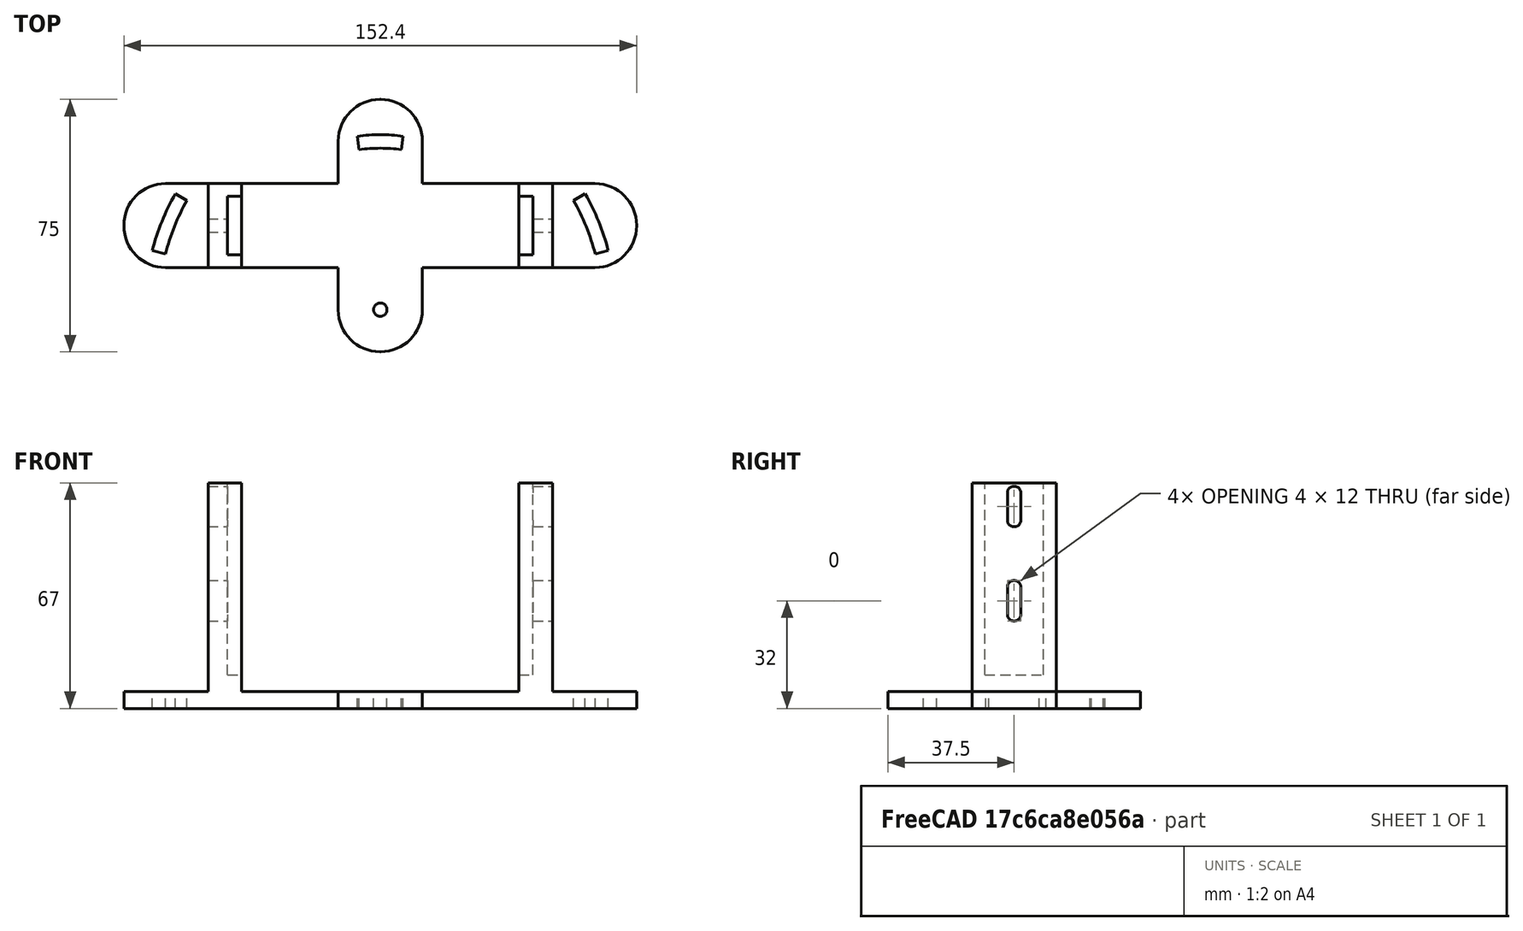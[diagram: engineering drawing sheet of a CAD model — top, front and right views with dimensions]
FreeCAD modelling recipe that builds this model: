
FCSTD DOCUMENT  (FreeCAD 0.18R4 (GitTag))
Label: Kamerhalter_Teil_4
License: All rights reserved
LicenseURL: http://en.wikipedia.org/wiki/All_rights_reserved
objects: Part::Box×10, Part::Cylinder×7, Part::Cut×6, Part::Fillet×6, Part::MultiFuse×5
note: 34 computed .brp shape members not serialized (recipe doc carries the construction recipe); baked Part::Feature solids carry a one-line shape summary decoded from their .brp

FEATURE [Part::Cylinder] Cylinder001  label="Zylinder001"
  Angle = 15
  AttacherType = Attacher::AttachEngine3D
  Height = 5
  Placement = pos=(0,0,0) rot=(0,0,1;0.253073rad)
  Radius = 70
FEATURE [Part::Cylinder] Cylinder002  label="Zylinder002"
  Angle = 15
  AttacherType = Attacher::AttachEngine3D
  Height = 5
  Placement = pos=(0,0,0) rot=(0,0,1;0.253073rad)
  Radius = 66
FEATURE [Part::Cut] Cut  label="Bohrschlitz001"
  Base = -> Cylinder001
  Tool = -> Cylinder002
FEATURE [Part::Cylinder] Cylinder003  label="Zylinder003"
  Angle = 15
  AttacherType = Attacher::AttachEngine3D
  Height = 5
  Placement = pos=(0,0,0) rot=(0,0,1;1.4399rad)
  Radius = 52
FEATURE [Part::Cylinder] Cylinder004  label="Zylinder004"
  Angle = 15
  AttacherType = Attacher::AttachEngine3D
  Height = 5
  Placement = pos=(0,0,0) rot=(0,0,1;1.4399rad)
  Radius = 48
FEATURE [Part::Cut] Cut001  label="Bohrschlitz002"
  Base = -> Cylinder003
  Tool = -> Cylinder004
FEATURE [Part::Cylinder] Cylinder005  label="Zylinder005"
  Angle = 15
  AttacherType = Attacher::AttachEngine3D
  Height = 5
  Placement = pos=(0,0,0) rot=(0,0,1;2.62672rad)
  Radius = 70
FEATURE [Part::Cylinder] Cylinder006  label="Zylinder006"
  Angle = 15
  AttacherType = Attacher::AttachEngine3D
  Height = 5
  Placement = pos=(0,0,0) rot=(0,0,1;2.62672rad)
  Radius = 66
FEATURE [Part::Cut] Cut002  label="Bohrschlitz003"
  Base = -> Cylinder005
  Tool = -> Cylinder006
FEATURE [Part::Box] Box006  label="Würfel006"
  AttacherType = Attacher::AttachEngine3D
  Height = 67
  Length = 10
  Placement = pos=(35,12.5,0) rot=(0,0,1;0rad)
  Width = 25
FEATURE [Part::Box] Box007  label="Würfel007"
  AttacherType = Attacher::AttachEngine3D
  Height = 67
  Length = 4.2
  Placement = pos=(35,16.3,10) rot=(0,0,1;0rad)
  Width = 17.4
FEATURE [Part::Box] Box008  label="Würfel008"
  AttacherType = Attacher::AttachEngine3D
  Height = 12
  Length = 6
  Placement = pos=(39,23,54) rot=(0,0,1;0rad)
  Width = 4
FEATURE [Part::Box] Box009  label="Würfel009"
  AttacherType = Attacher::AttachEngine3D
  Height = 12
  Length = 6
  Placement = pos=(39,23,26) rot=(0,0,1;0rad)
  Width = 4
FEATURE [Part::Fillet] Fillet006
  Base = -> Box008
  Edges = 4 edges r=1.9: [Edge9,Edge10,Edge11,Edge12]
FEATURE [Part::Fillet] Fillet007
  Base = -> Box009
  Edges = 4 edges r=1.9: [Edge9,Edge10,Edge11,Edge12]
FEATURE [Part::Box] Box010  label="Würfel010"
  AttacherType = Attacher::AttachEngine3D
  Height = 12
  Length = 6
  Placement = pos=(-45,23,54) rot=(0,0,1;0rad)
  Width = 4
FEATURE [Part::Box] Box011  label="Würfel011"
  AttacherType = Attacher::AttachEngine3D
  Height = 12
  Length = 6
  Placement = pos=(-45,23,26) rot=(0,0,1;0rad)
  Width = 4
FEATURE [Part::Fillet] Fillet008
  Base = -> Box010
  Edges = 4 edges r=1.9: [Edge9,Edge10,Edge11,Edge12]
FEATURE [Part::Fillet] Fillet009
  Base = -> Box011
  Edges = 4 edges r=1.9: [Edge9,Edge10,Edge11,Edge12]
FEATURE [Part::Box] Box012  label="Würfel012"
  AttacherType = Attacher::AttachEngine3D
  Height = 67
  Length = 10
  Placement = pos=(-45,12.5,0) rot=(0,0,1;0rad)
  Width = 25
FEATURE [Part::Box] Box013  label="Würfel013"
  AttacherType = Attacher::AttachEngine3D
  Height = 67
  Length = 4.2
  Placement = pos=(-39.2,16.3,10) rot=(0,0,1;0rad)
  Width = 17.4
FEATURE [Part::MultiFuse] Fusion002
  Shapes = -> [Fillet007,Box007,Fillet006]
FEATURE [Part::Cut] Cut005  label="Stuetze001"
  Base = -> Box006
  Placement = pos=(6.2,0,0) rot=(0,0,1;0rad)
  Tool = -> Fusion002
FEATURE [Part::MultiFuse] Fusion003
  Shapes = -> [Fillet008,Fillet009,Box013]
FEATURE [Part::Cut] Cut006  label="Stuetze002"
  Base = -> Box012
  Placement = pos=(-6.2,0,0) rot=(0,0,1;0rad)
  Tool = -> Fusion003
FEATURE [Part::Box] Box014  label="Würfel014"
  AttacherType = Attacher::AttachEngine3D
  Height = 5
  Length = 152.4
  Placement = pos=(-76.2,12.5,0) rot=(0,0,1;0rad)
  Width = 25
FEATURE [Part::Fillet] Fillet010  label="Fillet001"
  Base = -> Box014
  Edges = 4 edges r=12.4: [Edge1,Edge3,Edge5,Edge7]
FEATURE [Part::Box] Box015  label="Würfel015"
  AttacherType = Attacher::AttachEngine3D
  Height = 5
  Length = 25
  Placement = pos=(-12.5,-12.5,0) rot=(0,0,1;0rad)
  Width = 75
FEATURE [Part::Fillet] Fillet011  label="Fillet002"
  Base = -> Box015
  Edges = 4 edges r=12.4: [Edge1,Edge3,Edge5,Edge7]
FEATURE [Part::MultiFuse] Fusion005  label="Sockel"
  Shapes = -> [Fillet010,Fillet011]
FEATURE [Part::Cylinder] Cylinder007  label="Borhloch002"
  Angle = 360
  AttacherType = Attacher::AttachEngine3D
  Height = 5
  Radius = 2
FEATURE [Part::MultiFuse] Fusion004  label="Bohrschlitze_Sockel"
  Shapes = -> [Cut002,Cut,Cut001,Cylinder007]
FEATURE [Part::Cut] Cut007
  Base = -> Fusion005
  Tool = -> Fusion004
FEATURE [Part::MultiFuse] Fusion  label="Teil_4"
  Shapes = -> [Cut007,Cut006,Cut005]
